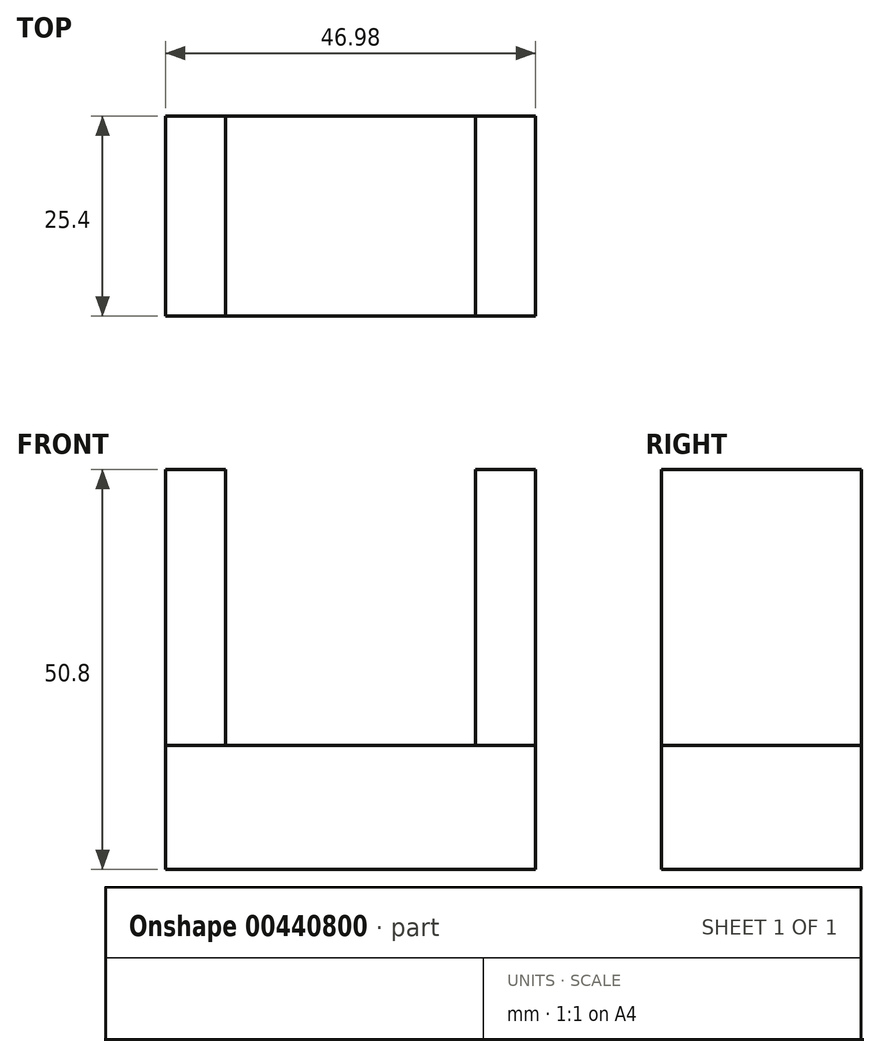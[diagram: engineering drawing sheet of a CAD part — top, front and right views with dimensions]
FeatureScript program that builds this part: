
annotation { "Feature Type Name" : "Feature", "Feature Type Description" : "" }
export const myFeature = defineFeature(function(context is Context, id is Id, definition is map)
    precondition{}
    {
        {
            var Q0;
            Q0=qCreatedBy(makeId("Top.planeOp"),FACE);
            var sketch = newSketch(context, id + "F0", { "sketchPlane" : qUnion([Q0])});
            skLineSegment(sketch, "E0.bottom", {"start": v(15.88, 12.7) * mm, "end": v(-15.88, 12.7) * mm});
            skLineSegment(sketch, "E0.top", {"start": v(15.88, -12.7) * mm, "end": v(-15.88, -12.7) * mm});
            skLineSegment(sketch, "E0.left", {"start": v(15.88, 12.7) * mm, "end": v(15.88, -12.7) * mm});
            skLineSegment(sketch, "E0.right", {"start": v(-15.88, 12.7) * mm, "end": v(-15.88, -12.7) * mm});
            skPoint(sketch, "E0.middle", {"position": v(0, 0) * mm});
            skLineSegment(sketch, "E1.bottom", {"start": v(-15.88, 12.7) * mm, "end": v(-23.5, 12.7) * mm});
            skLineSegment(sketch, "E1.top", {"start": v(-15.87, -12.7) * mm, "end": v(-23.5, -12.7) * mm});
            skLineSegment(sketch, "E1.right", {"start": v(-23.5, 12.7) * mm, "end": v(-23.5, -12.7) * mm});
            skLineSegment(sketch, "E2.MirrorCS", {"start": v(15.88, 12.7) * mm, "end": v(23.5, 12.7) * mm});
            skLineSegment(sketch, "E3.MirrorCS", {"start": v(23.5, 12.7) * mm, "end": v(23.5, -12.7) * mm});
            skLineSegment(sketch, "E4.MirrorCS", {"start": v(15.87, -12.7) * mm, "end": v(23.5, -12.7) * mm});
            skSolve(sketch);
        }
        {
            var Q0;
            Q0=makeQuery(id+"F0.imprint","IMPRINT",FACE,{"disambiguationData":[TD([[makeQuery(id+"F0.imprint","IMPRINT",EDGE,{"derivedFrom":sQuery(id+"F0.wireOp",EDGE,"E1.bottom")}),1.0]])]});
            var Q1;
            Q1=makeQuery(id+"F0.imprint","IMPRINT",FACE,{"disambiguationData":[TD([[makeQuery(id+"F0.imprint","IMPRINT",EDGE,{"derivedFrom":sQuery(id+"F0.wireOp",EDGE,"E2.MirrorCS")}),-1.0]])]});
            extrude(context, id + "F1", {"entities" : qUnion([Q0, Q1]), "depth" : 35.05 * mm});
        }
        {
            var Q0;
            Q0=makeQuery(id+"F0.imprint","IMPRINT",FACE,{"disambiguationData":[TD([[makeQuery(id+"F0.imprint","IMPRINT",EDGE,{"derivedFrom":sQuery(id+"F0.wireOp",EDGE,"E1.bottom")}),1.0]])]});
            var Q1;
            Q1=makeQuery(id+"F0.imprint","IMPRINT",FACE,{"disambiguationData":[TD([[makeQuery(id+"F0.imprint","IMPRINT",EDGE,{"derivedFrom":sQuery(id+"F0.wireOp",EDGE,"E2.MirrorCS")}),-1.0]])]});
            var Q2;
            Q2=makeQuery(id+"F0.imprint","IMPRINT",FACE,{"disambiguationData":[TD([[makeQuery(id+"F0.imprint","IMPRINT",EDGE,{"derivedFrom":sQuery(id+"F0.wireOp",EDGE,"E0.bottom")}),1.0]])]});
            extrude(context, id + "F2", {"entities" : qUnion([Q0, Q1, Q2]), "oppositeDirection" : true, "depth" : 15.75 * mm});
        }
    });
